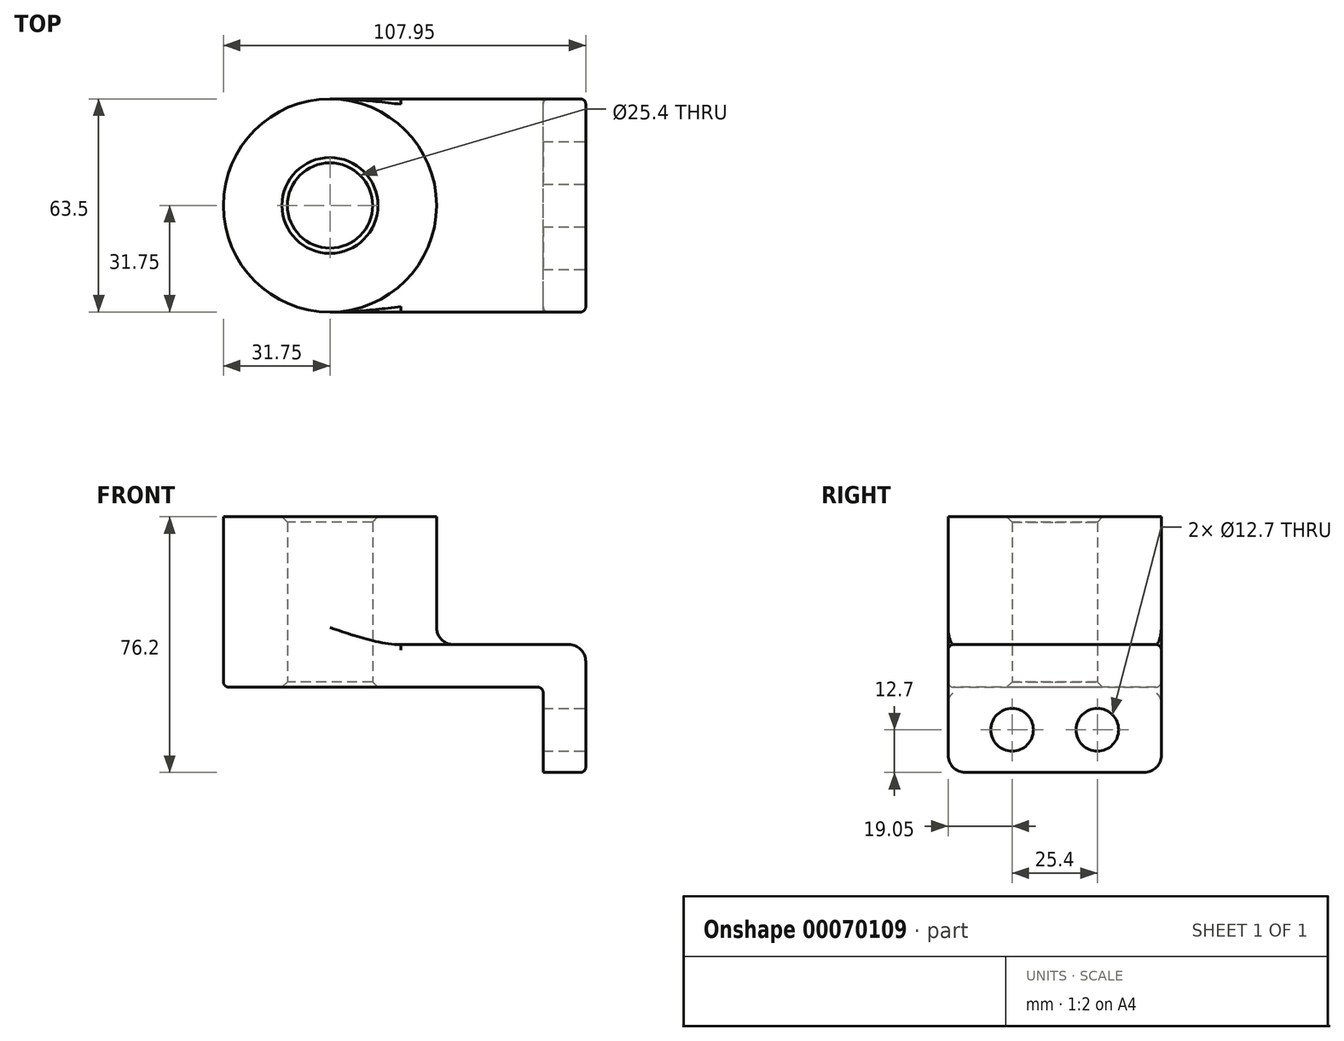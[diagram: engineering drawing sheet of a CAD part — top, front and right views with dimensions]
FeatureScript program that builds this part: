
annotation { "Feature Type Name" : "Feature", "Feature Type Description" : "" }
export const myFeature = defineFeature(function(context is Context, id is Id, definition is map)
    precondition{}
    {
        {
            var Q0;
            Q0=qCreatedBy(makeId("Top.planeOp"),FACE);
            var sketch = newSketch(context, id + "F0", { "sketchPlane" : qUnion([Q0])});
            skLineSegment(sketch, "E0.bottom", {"start": v(38.1, -31.75) * mm, "end": v(-38.1, -31.75) * mm});
            skLineSegment(sketch, "E0.top", {"start": v(38.1, 31.75) * mm, "end": v(-38.1, 31.75) * mm});
            skLineSegment(sketch, "E0.left", {"start": v(38.1, -31.75) * mm, "end": v(38.1, 31.75) * mm});
            skLineSegment(sketch, "E0.right", {"start": v(-38.1, -31.75) * mm, "end": v(-38.1, 31.75) * mm});
            skPoint(sketch, "E0.middle", {"position": v(0, 0) * mm});
            skCircle(sketch, "E1", {"center": v(-38.1, 0) * mm, "radius": 31.75 * mm});
            skCircle(sketch, "E2", {"center": v(-38.1, 0) * mm, "radius": 12.7 * mm});
            skSolve(sketch);
        }
        {
            var Q0;
            Q0 = qSketchRegion(id + "F0", true);
            extrude(context, id + "F1", {"entities" : qUnion([Q0]), "depth" : 12.7 * mm});
        }
        {
            var Q0;
            {var subQ1=sQuery(id+"F0.wireOp",EDGE,"E0.right");var subQ3=sQuery(id+"F0.wireOp",EDGE,"E2");var subQ4=makeQuery(id+"F0.imprint","INTERSECT",VERTEX,{"disambiguationData":[OD(0.0)],"derivedFrom":[subQ1,subQ3]});Q0=makeQuery(id+"F0.imprint","IMPRINT",FACE,{"disambiguationData":[TD([[makeQuery(id+"F0.imprint","IMPRINT",EDGE,{"disambiguationData":[TD([[subQ4,1.0]])],"derivedFrom":subQ3}),-1.0]])]});}
            var Q1;
            {var subQ1=sQuery(id+"F0.wireOp",EDGE,"E0.right");var subQ3=sQuery(id+"F0.wireOp",EDGE,"E2");var subQ4=makeQuery(id+"F0.imprint","INTERSECT",VERTEX,{"disambiguationData":[OD(0.0)],"derivedFrom":[subQ1,subQ3]});Q1=makeQuery(id+"F0.imprint","IMPRINT",FACE,{"disambiguationData":[TD([[makeQuery(id+"F0.imprint","IMPRINT",EDGE,{"disambiguationData":[TD([[subQ4,-1.0]])],"derivedFrom":subQ3}),-1.0]])]});}
            extrude(context, id + "F2", {"entities" : qUnion([Q0, Q1]), "operationType" : NewBodyOperationType.ADD, "depth" : 50.8 * mm});
        }
        {
            var Q0;
            Q0=makeQuery(id+"F1.opExtrude","SWEPT_FACE",FACE,{"disambiguationData":[OSD([sQuery(id+"F0.wireOp",EDGE,"E0.left")])]});
            var sketch = newSketch(context, id + "F3", { "sketchPlane" : qUnion([Q0])});
            skLineSegment(sketch, "E3.bottom", {"start": v(-31.75, 12.7) * mm, "end": v(31.75, 12.7) * mm});
            skLineSegment(sketch, "E3.top", {"start": v(-31.75, -25.4) * mm, "end": v(31.75, -25.4) * mm});
            skLineSegment(sketch, "E3.left", {"start": v(-31.75, 12.7) * mm, "end": v(-31.75, -25.4) * mm});
            skLineSegment(sketch, "E3.right", {"start": v(31.75, 12.7) * mm, "end": v(31.75, -25.4) * mm});
            skLineSegment(sketch, "E4", {"start": v(0, 0) * mm, "end": v(0, -25.4) * mm, "construction": true});
            skCircle(sketch, "E5.MirrorC", {"center": v(12.7, -12.7) * mm, "radius": 6.35 * mm});
            skCircle(sketch, "E6.MirrorC", {"center": v(-12.7, -12.7) * mm, "radius": 6.35 * mm});
            skSolve(sketch);
        }
        {
            var Q0;
            Q0 = qSketchRegion(id + "F3", true);
            extrude(context, id + "F4", {"entities" : qUnion([Q0]), "operationType" : NewBodyOperationType.ADD, "oppositeDirection" : true, "depth" : 12.7 * mm});
        }
        {
            var Q0;
            {var subQ0=sQuery(id+"F0.wireOp",EDGE,"E1");Q0=makeQuery(id+"F2.boolean.opBoolean","INTERSECT",EDGE,{"derivedFrom":[makeQuery(id+"F1.opExtrude","CAP_FACE",FACE,{"disambiguationData":[OSD([sQuery(id+"F0.wireOp",EDGE,"E0.bottom"),sQuery(id+"F0.wireOp",EDGE,"E0.top"),sQuery(id+"F0.wireOp",EDGE,"E0.left"),subQ0,sQuery(id+"F0.wireOp",EDGE,"E2")])],"isStart":false}),makeQuery(id+"F2.opExtrude","SWEPT_FACE",FACE,{"disambiguationData":[OSD([subQ0])]})]});}
            var Q1;
            Q1=makeQuery(id+"F1.opExtrude","CAP_EDGE",EDGE,{"disambiguationData":[OSD([sQuery(id+"F0.wireOp",EDGE,"E0.left")])],"isStart":false});
            var Q2;
            Q2=makeQuery(id+"F4.opExtrude","SWEPT_EDGE",EDGE,{"disambiguationData":[OSD([sQuery(id+"F3.wireOp",EDGE,"E3.top"),sQuery(id+"F3.wireOp",EDGE,"E3.left")])]});
            var Q3;
            Q3=makeQuery(id+"F4.opExtrude","SWEPT_EDGE",EDGE,{"disambiguationData":[OSD([sQuery(id+"F3.wireOp",EDGE,"E3.top"),sQuery(id+"F3.wireOp",EDGE,"E3.right")])]});
            fillet(context, id + "F5", {"entities" : qUnion([Q0, Q1, Q2, Q3]), "radius" : 5.08 * mm, "tangentPropagation" : true, "allowEdgeOverflow" : false});
        }
        {
            var Q0;
            Q0=makeQuery(id+"F1.opExtrude","CAP_EDGE",EDGE,{"disambiguationData":[OSD([sQuery(id+"F0.wireOp",EDGE,"E0.bottom")])],"isStart":false});
            var Q1;
            Q1=makeQuery(id+"F1.opExtrude","CAP_EDGE",EDGE,{"disambiguationData":[OSD([sQuery(id+"F0.wireOp",EDGE,"E0.bottom")])],"isStart":true});
            var Q2;
            Q2=makeQuery(id+"F4.boolean.opBoolean","INTERSECT",EDGE,{"derivedFrom":[makeQuery(id+"F1.opExtrude","CAP_FACE",FACE,{"disambiguationData":[OSD([sQuery(id+"F0.wireOp",EDGE,"E0.bottom"),sQuery(id+"F0.wireOp",EDGE,"E0.top"),sQuery(id+"F0.wireOp",EDGE,"E0.left"),sQuery(id+"F0.wireOp",EDGE,"E1"),sQuery(id+"F0.wireOp",EDGE,"E2")])],"isStart":true}),makeQuery(id+"F4.opExtrude","CAP_FACE",FACE,{"disambiguationData":[OSD([sQuery(id+"F3.wireOp",EDGE,"E3.bottom"),sQuery(id+"F3.wireOp",EDGE,"E3.top"),sQuery(id+"F3.wireOp",EDGE,"E3.left"),sQuery(id+"F3.wireOp",EDGE,"E3.right"),sQuery(id+"F3.wireOp",EDGE,"E5.MirrorC"),sQuery(id+"F3.wireOp",EDGE,"E6.MirrorC")])],"isStart":false})]});
            fillet(context, id + "F6", {"entities" : qUnion([Q0, Q1, Q2]), "radius" : 1.59 * mm, "tangentPropagation" : true, "allowEdgeOverflow" : false});
        }
        {
            var Q0;
            {var subQ0=sQuery(id+"F0.wireOp",EDGE,"E2");Q0=makeQuery(id+"F2.boolean.opBoolean","MERGE",FACE,{"derivedFrom":[makeQuery(id+"F1.opExtrude","SWEPT_FACE",FACE,{"disambiguationData":[OSD([subQ0])]}),makeQuery(id+"F2.opExtrude","SWEPT_FACE",FACE,{"disambiguationData":[OSD([subQ0])]})]});}
            chamfer(context, id + "F7", {"entities" : qUnion([Q0]), "width" : 1.59 * mm, "tangentPropagation" : true});
        }
    });
